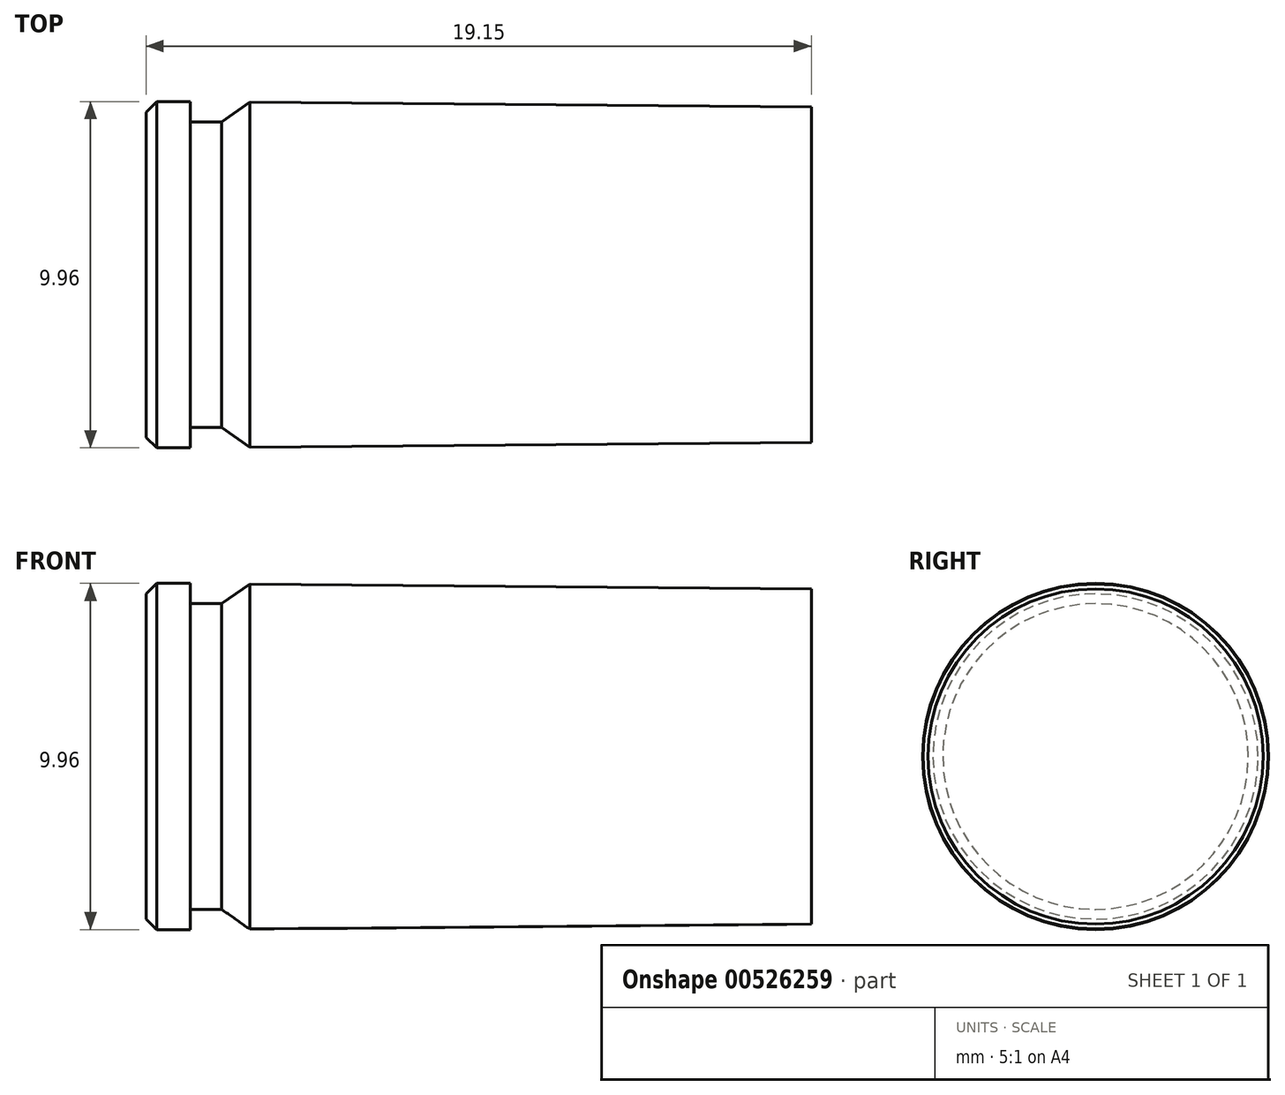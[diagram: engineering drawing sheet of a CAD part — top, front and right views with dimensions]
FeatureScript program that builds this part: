
annotation { "Feature Type Name" : "Feature", "Feature Type Description" : "" }
export const myFeature = defineFeature(function(context is Context, id is Id, definition is map)
    precondition{}
    {
        {
            var Q0;
            Q0=qCreatedBy(makeId("Front.planeOp"),FACE);
            var sketch = newSketch(context, id + "F0", { "sketchPlane" : qUnion([Q0])});
            skLineSegment(sketch, "E0", {"start": v(16.17, 4.83) * mm, "end": v(16.17, 0) * mm});
            skLineSegment(sketch, "E1", {"start": v(0, 4.97) * mm, "end": v(16.17, 4.82) * mm});
            skPoint(sketch, "E2", {"position": v(16.17, 0) * mm});
            skLineSegment(sketch, "E3", {"start": v(0, 4.96) * mm, "end": v(-0.8, 4.4) * mm});
            skPoint(sketch, "E4", {"position": v(-0.8, 0) * mm});
            skPoint(sketch, "E5", {"position": v(-1.7, 0) * mm});
            skPoint(sketch, "E6", {"position": v(-2.68, 0) * mm});
            skPoint(sketch, "E7", {"position": v(-2.98, 0) * mm});
            skLineSegment(sketch, "E8", {"start": v(-0.8, 0) * mm, "end": v(-0.8, 4.4) * mm});
            skLineSegment(sketch, "E9", {"start": v(-0.8, 4.4) * mm, "end": v(-1.7, 4.4) * mm});
            skLineSegment(sketch, "E10", {"start": v(-1.7, 0) * mm, "end": v(-1.7, 4.4) * mm});
            skLineSegment(sketch, "E11", {"start": v(-2.68, 4.98) * mm, "end": v(-1.7, 4.98) * mm});
            skLineSegment(sketch, "E12", {"start": v(-1.7, 4.98) * mm, "end": v(-1.7, 4.4) * mm});
            skLineSegment(sketch, "E13", {"start": v(-2.68, 4.98) * mm, "end": v(-2.98, 4.68) * mm});
            skLineSegment(sketch, "E14", {"start": v(-2.98, 0) * mm, "end": v(-2.98, 4.68) * mm});
            skPoint(sketch, "E15", {"position": v(26.71, 0) * mm});
            skPoint(sketch, "E16", {"position": v(16.17, 4.51) * mm});
            skPoint(sketch, "E17", {"position": v(16.17, -4.51) * mm});
            skLineSegment(sketch, "E18", {"start": v(30.22, 0) * mm, "end": v(-19.16, 0) * mm});
            skPoint(sketch, "E19.trimOffspring.end.orphan", {"position": v(16.17, -4.83) * mm});
            skPoint(sketch, "E20.end.orphan", {"position": v(-1.7, -4.4) * mm});
            skPoint(sketch, "E21.end.orphan", {"position": v(-1.7, -4.98) * mm});
            skPoint(sketch, "E22.start.orphan", {"position": v(-2.68, -4.98) * mm});
            skSolve(sketch);
        }
        {
            var Q0;
            Q0 = qSketchRegion(id + "F0", true);
            var Q1;
            Q1=sQuery(id+"F0.wireOp",EDGE,"E18");
            revolve(context, id + "F1", {"entities" : qUnion([Q0]), "axis" : qUnion([Q1]), "revolveType" : RevolveType.FULL});
        }
    });
